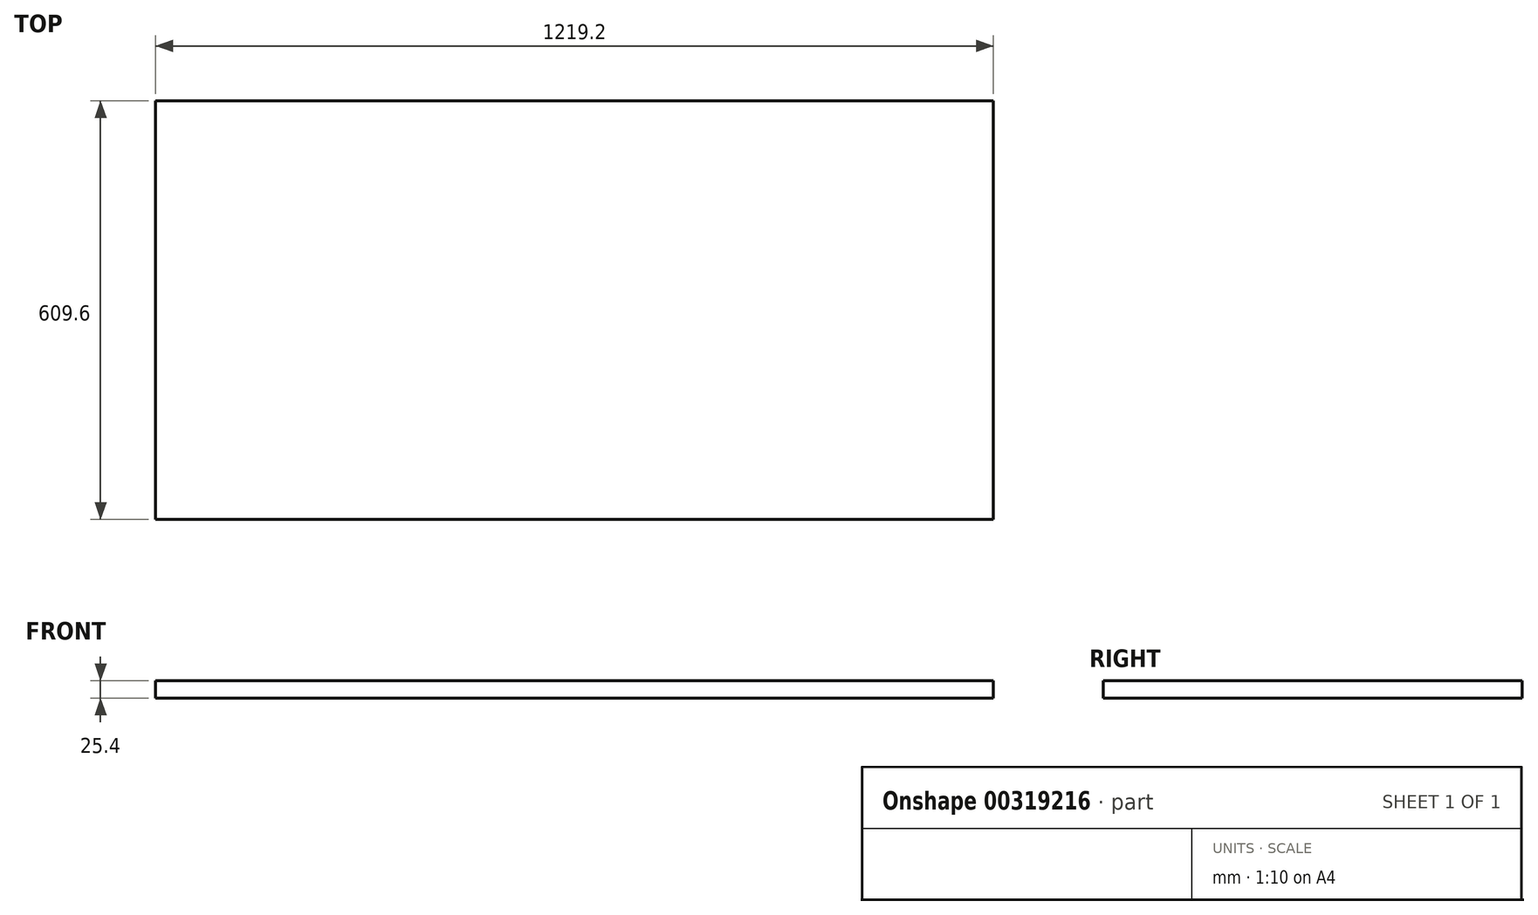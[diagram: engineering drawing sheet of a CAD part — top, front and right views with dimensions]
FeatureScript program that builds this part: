
annotation { "Feature Type Name" : "Feature", "Feature Type Description" : "" }
export const myFeature = defineFeature(function(context is Context, id is Id, definition is map)
    precondition{}
    {
        {
            var Q0;
            Q0=qCreatedBy(makeId("Top.planeOp"),FACE);
            var sketch = newSketch(context, id + "F0", { "sketchPlane" : qUnion([Q0])});
            skLineSegment(sketch, "E0.bottom", {"start": v(-811.1, 668.47) * mm, "end": v(408.1, 668.47) * mm});
            skLineSegment(sketch, "E0.top", {"start": v(-811.1, 58.87) * mm, "end": v(408.1, 58.87) * mm});
            skLineSegment(sketch, "E0.left", {"start": v(-811.1, 668.47) * mm, "end": v(-811.1, 58.87) * mm});
            skLineSegment(sketch, "E0.right", {"start": v(408.1, 668.47) * mm, "end": v(408.1, 58.87) * mm});
            skSolve(sketch);
        }
        {
            var Q0;
            Q0=makeQuery(id+"F0.imprint","IMPRINT",FACE,{"disambiguationData":[TD([[makeQuery(id+"F0.imprint","IMPRINT",EDGE,{"derivedFrom":sQuery(id+"F0.wireOp",EDGE,"E0.bottom")}),-1.0]])]});
            var sketch = newSketch(context, id + "F1", { "sketchPlane" : qUnion([Q0])});
            skSolve(sketch);
        }
        {
            var Q0;
            Q0 = qSketchRegion(id + "F1", true);
            var Q1;
            Q1=makeQuery(id+"F0.imprint","IMPRINT",FACE,{"disambiguationData":[TD([[makeQuery(id+"F0.imprint","IMPRINT",EDGE,{"derivedFrom":sQuery(id+"F0.wireOp",EDGE,"E0.bottom")}),-1.0]])]});
            extrude(context, id + "F2", {"entities" : qUnion([Q0, Q1]), "depth" : 25.4 * mm});
        }
    });
